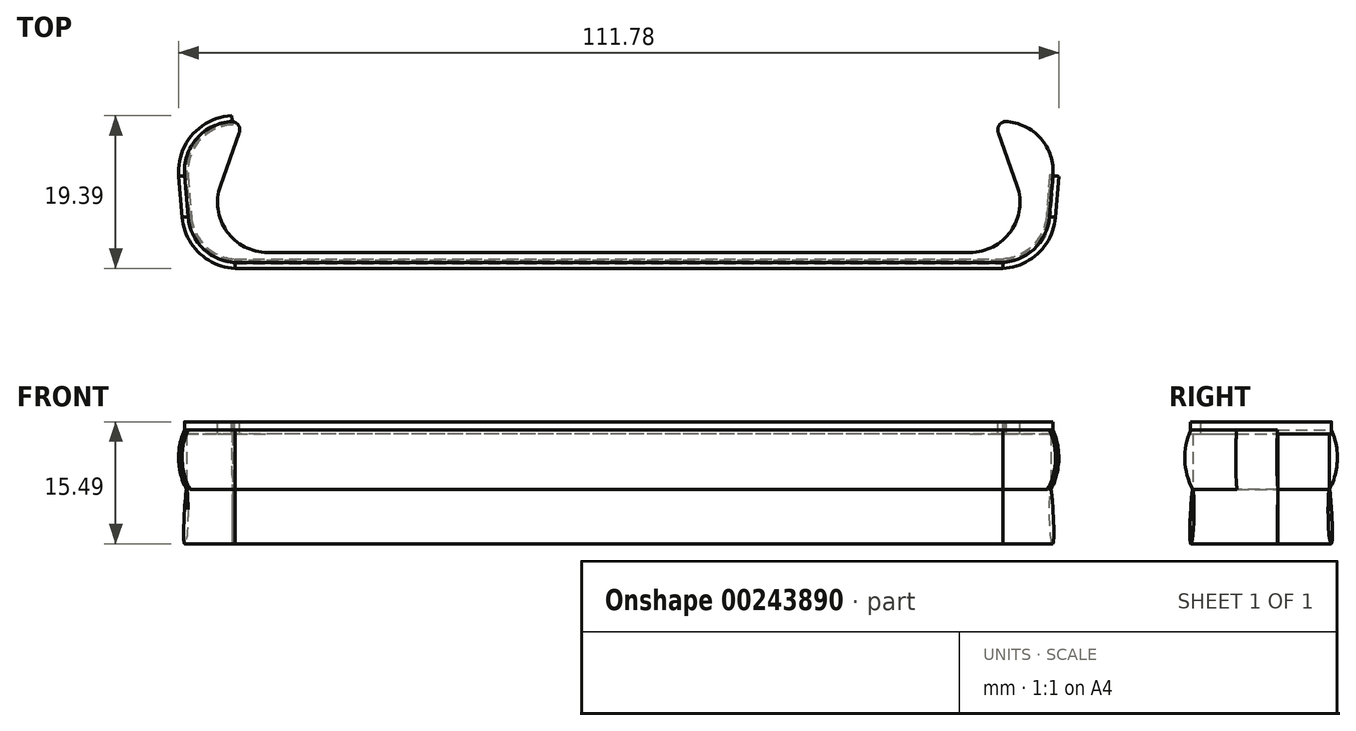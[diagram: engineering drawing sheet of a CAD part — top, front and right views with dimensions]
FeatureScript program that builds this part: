
annotation { "Feature Type Name" : "Feature", "Feature Type Description" : "" }
export const myFeature = defineFeature(function(context is Context, id is Id, definition is map)
    precondition{}
    {
        {
            var Q0;
            Q0=qCreatedBy(makeId("Top.planeOp"),FACE);
            var sketch = newSketch(context, id + "F0", { "sketchPlane" : qUnion([Q0])});
            skLineSegment(sketch, "E0", {"start": v(-44.61, 0) * mm, "end": v(0, 0) * mm});
            skLineSegment(sketch, "E1", {"start": v(-54.73, 4.56) * mm, "end": v(-55.15, 9.77) * mm});
            skLineSegment(sketch, "E2", {"start": v(-49.22, 16.63) * mm, "end": v(-48.82, 16.63) * mm});
            skLineSegment(sketch, "E3", {"start": v(-48.2, 15.2) * mm, "end": v(-50.6, 8.48) * mm});
            skLineSegment(sketch, "E4", {"start": v(0, -1.28) * mm, "end": v(-48.4, -1.28) * mm});
            skPoint(sketch, "E5.visualSharp", {"position": v(-54.26, -1.28) * mm});
            skArc(sketch, "E5.filletArc", {"start": v(-54.73, 4.56) * mm, "mid": v(-52.7, 0.4) * mm, "end": v(-48.4, -1.28) * mm});
            skPoint(sketch, "E6.visualSharp", {"position": v(-53.6, 0) * mm});
            skArc(sketch, "E6.filletArc", {"start": v(-50.6, 8.48) * mm, "mid": v(-49.8, 2.69) * mm, "end": v(-44.61, 0) * mm});
            skPoint(sketch, "E7.visualSharp", {"position": v(-55.7, 16.63) * mm});
            skArc(sketch, "E7.filletArc", {"start": v(-48.82, 16.63) * mm, "mid": v(-53.49, 14.6) * mm, "end": v(-55.15, 9.77) * mm});
            skPoint(sketch, "E8.visualSharp", {"position": v(-47.7, 16.63) * mm});
            skArc(sketch, "E8.filletArc", {"start": v(-48.2, 15.2) * mm, "mid": v(-48.34, 16.18) * mm, "end": v(-49.22, 16.63) * mm});
            skArc(sketch, "E9.MirrorCS", {"start": v(48.2, 15.2) * mm, "mid": v(48.34, 16.18) * mm, "end": v(49.22, 16.63) * mm});
            skLineSegment(sketch, "E10.MirrorCS", {"start": v(49.22, 16.63) * mm, "end": v(48.82, 16.63) * mm});
            skArc(sketch, "E11.MirrorCS", {"start": v(54.73, 4.56) * mm, "mid": v(52.7, 0.4) * mm, "end": v(48.4, -1.28) * mm});
            skArc(sketch, "E12.MirrorCS", {"start": v(50.6, 8.48) * mm, "mid": v(49.8, 2.69) * mm, "end": v(44.61, 0) * mm});
            skPoint(sketch, "E13.MirrorP", {"position": v(47.7, 16.63) * mm});
            skLineSegment(sketch, "E14.MirrorCS", {"start": v(54.73, 4.56) * mm, "end": v(55.15, 9.77) * mm});
            skArc(sketch, "E15.MirrorCS", {"start": v(48.82, 16.63) * mm, "mid": v(53.49, 14.6) * mm, "end": v(55.15, 9.77) * mm});
            skLineSegment(sketch, "E16.MirrorCS", {"start": v(44.61, 0) * mm, "end": v(0, 0) * mm});
            skPoint(sketch, "E17.MirrorP", {"position": v(54.26, -1.28) * mm});
            skPoint(sketch, "E18.MirrorP", {"position": v(53.6, 0) * mm});
            skLineSegment(sketch, "E19.MirrorCS", {"start": v(0, -1.28) * mm, "end": v(48.4, -1.28) * mm});
            skPoint(sketch, "E20.MirrorP", {"position": v(55.7, 16.63) * mm});
            skLineSegment(sketch, "E21.MirrorCS", {"start": v(48.2, 15.2) * mm, "end": v(50.6, 8.48) * mm});
            skLineSegment(sketch, "E22", {"start": v(-50.96, 6.12) * mm, "end": v(50.96, 6.12) * mm});
            skSolve(sketch);
        }
        {
            var Q0;
            Q0 = qSketchRegion(id + "F0", true);
            extrude(context, id + "F1", {"entities" : qUnion([Q0]), "oppositeDirection" : true, "depth" : 1.52 * mm});
        }
        {
            var Q0;
            Q0=qCreatedBy(makeId("Right.planeOp"),FACE);
            var sketch = newSketch(context, id + "F2", { "sketchPlane" : qUnion([Q0])});
            skLineSegment(sketch, "E23", {"start": v(-1, -0.48) * mm, "end": v(-1, -8.6) * mm});
            skArc(sketch, "E24", {"start": v(-1, -0.48) * mm, "mid": v(-2.02, -4.54) * mm, "end": v(-1, -8.6) * mm});
            skFitSpline(sketch, "E25", {"points": [v(-1, -8.6) * mm, v(-1.3, -15.4) * mm, v(-1, -14.71) * mm, v(-1, -8.6) * mm]});
            skSolve(sketch);
        }
        {
            var Q0;
            Q0=makeQuery(id+"F2.imprint","IMPRINT",FACE,{"disambiguationData":[TD([[makeQuery(id+"F2.imprint","IMPRINT",EDGE,{"derivedFrom":sQuery(id+"F2.wireOp",EDGE,"E25")}),1.0]])]});
            var Q1;
            Q1=makeQuery(id+"F2.imprint","IMPRINT",FACE,{"disambiguationData":[TD([[makeQuery(id+"F2.imprint","IMPRINT",EDGE,{"derivedFrom":sQuery(id+"F2.wireOp",EDGE,"E23")}),-1.0]])]});
            extrude(context, id + "F3", {"entities" : qUnion([Q0, Q1]), "operationType" : NewBodyOperationType.ADD, "endBound" : BoundingType.SYMMETRIC, "depth" : 97.54 * mm});
        }
        {
            var Q0;
            Q0=makeQuery(id+"F3.opExtrude","CAP_FACE",FACE,{"disambiguationData":[OSD([sQuery(id+"F2.wireOp",EDGE,"E23"),sQuery(id+"F2.wireOp",EDGE,"E24")])],"isStart":false});
            var Q1;
            Q1=makeQuery(id+"F3.opExtrude","CAP_FACE",FACE,{"disambiguationData":[OSD([sQuery(id+"F2.wireOp",EDGE,"E25")])],"isStart":false});
            var Q2;
            Q2=makeQuery(id+"F1.opExtrude","CAP_EDGE",EDGE,{"disambiguationData":[OSD([sQuery(id+"F0.wireOp",EDGE,"E11.MirrorCS")])],"isStart":false});
            var Q3;
            Q3=makeQuery(id+"F1.opExtrude","CAP_EDGE",EDGE,{"disambiguationData":[OSD([sQuery(id+"F0.wireOp",EDGE,"E14.MirrorCS")])],"isStart":false});
            var Q4;
            {var subQ0=sQuery(id+"F0.wireOp",EDGE,"E15.MirrorCS");Q4=makeQuery(id+"F1.opExtrude","CAP_EDGE",EDGE,{"disambiguationData":[OSD([subQ0]),TDD([makeQuery(id+"F0.imprint","IMPRINT",EDGE,{"disambiguationData":[TD([[makeQuery(id+"F0.imprint","INTERSECT",VERTEX,{"derivedFrom":[sQuery(id+"F0.wireOp",EDGE,"E14.MirrorCS"),subQ0]}),1.0]])],"derivedFrom":subQ0})])],"isStart":false});}
            sweep(context, id + "F4", {"operationType" : NewBodyOperationType.ADD, "profiles" : qUnion([Q0, Q1]), "path" : qUnion([Q2, Q3, Q4])});
        }
        {
            var Q0;
            Q0=makeQuery(id+"F3.opExtrude","CAP_FACE",FACE,{"disambiguationData":[OSD([sQuery(id+"F2.wireOp",EDGE,"E23"),sQuery(id+"F2.wireOp",EDGE,"E24")])],"isStart":true});
            var Q1;
            Q1=makeQuery(id+"F3.opExtrude","CAP_FACE",FACE,{"disambiguationData":[OSD([sQuery(id+"F2.wireOp",EDGE,"E25")])],"isStart":true});
            var Q2;
            Q2=makeQuery(id+"F1.opExtrude","CAP_EDGE",EDGE,{"disambiguationData":[OSD([sQuery(id+"F0.wireOp",EDGE,"E5.filletArc")])],"isStart":false});
            var Q3;
            Q3=makeQuery(id+"F1.opExtrude","CAP_EDGE",EDGE,{"disambiguationData":[OSD([sQuery(id+"F0.wireOp",EDGE,"E1")])],"isStart":false});
            var Q4;
            {var subQ0=sQuery(id+"F0.wireOp",EDGE,"E7.filletArc");Q4=makeQuery(id+"F1.opExtrude","CAP_EDGE",EDGE,{"disambiguationData":[OSD([subQ0]),TDD([makeQuery(id+"F0.imprint","IMPRINT",EDGE,{"disambiguationData":[TD([[makeQuery(id+"F0.imprint","INTERSECT",VERTEX,{"derivedFrom":[sQuery(id+"F0.wireOp",EDGE,"E1"),subQ0]}),1.0]])],"derivedFrom":subQ0})])],"isStart":false});}
            sweep(context, id + "F5", {"operationType" : NewBodyOperationType.ADD, "profiles" : qUnion([Q0, Q1]), "path" : qUnion([Q2, Q3, Q4])});
        }
    });
